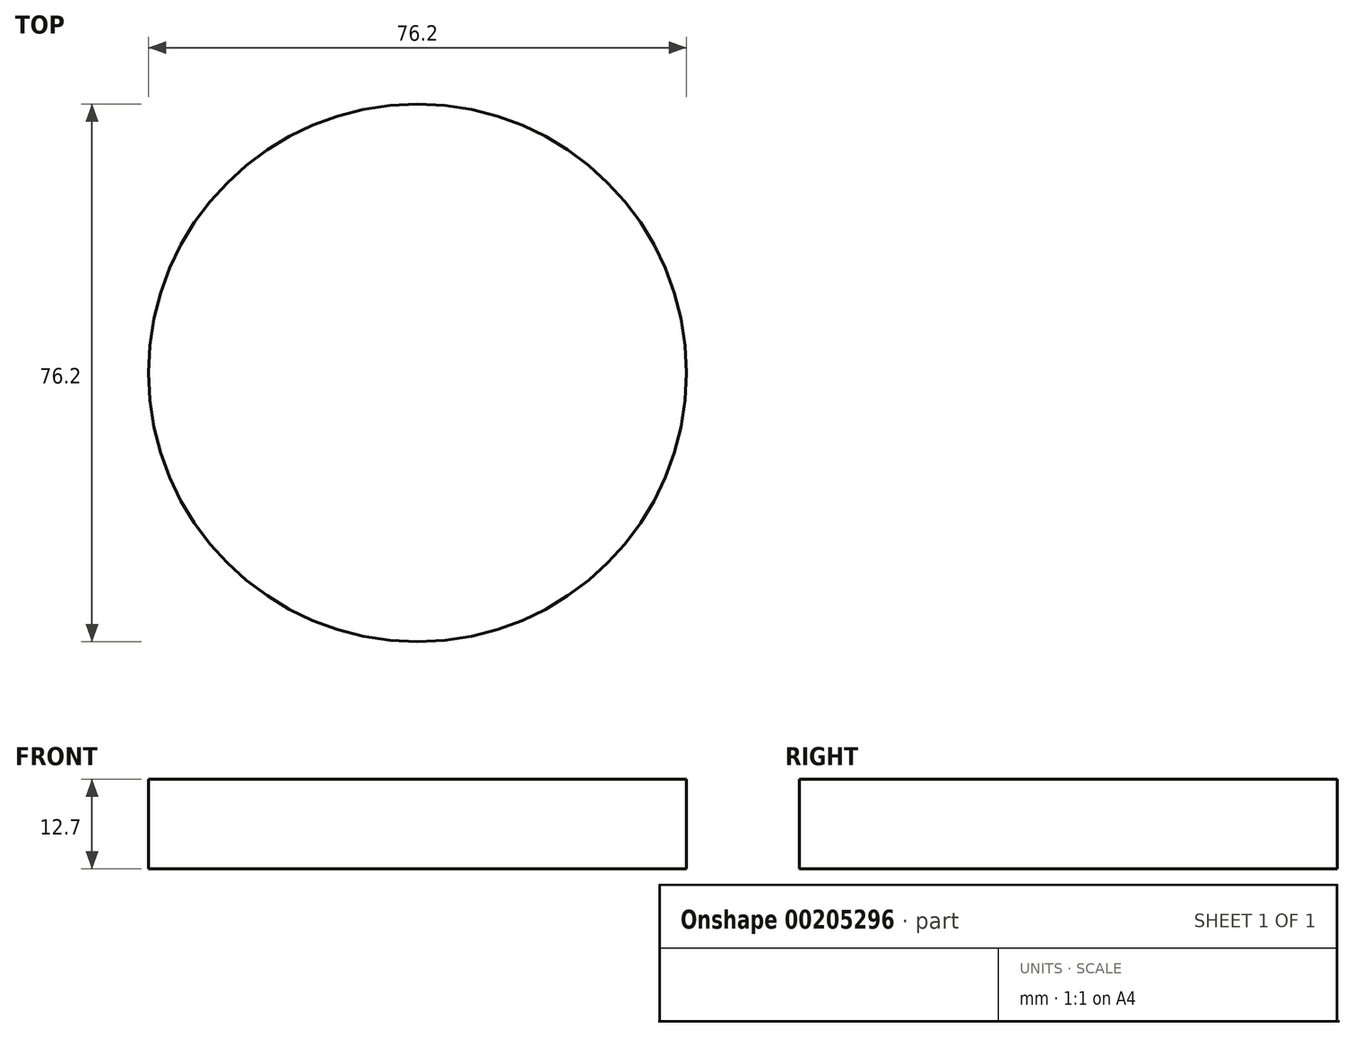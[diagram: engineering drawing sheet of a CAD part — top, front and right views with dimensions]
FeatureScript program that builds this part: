
annotation { "Feature Type Name" : "Feature", "Feature Type Description" : "" }
export const myFeature = defineFeature(function(context is Context, id is Id, definition is map)
    precondition{}
    {
        {
            var Q0;
            Q0=qCreatedBy(makeId("Top.planeOp"),FACE);
            var sketch = newSketch(context, id + "F0", { "sketchPlane" : qUnion([Q0])});
            skCircle(sketch, "E0", {"center": v(0, 0) * mm, "radius": 38.1 * mm});
            skSolve(sketch);
        }
        {
            var Q0;
            Q0=makeQuery(id+"F0.imprint","IMPRINT",FACE,{"disambiguationData":[TD([[makeQuery(id+"F0.imprint","IMPRINT",EDGE,{"derivedFrom":sQuery(id+"F0.wireOp",EDGE,"E0")}),1.0]])]});
            extrude(context, id + "F1", {"entities" : qUnion([Q0]), "depth" : 12.7 * mm});
        }
    });
